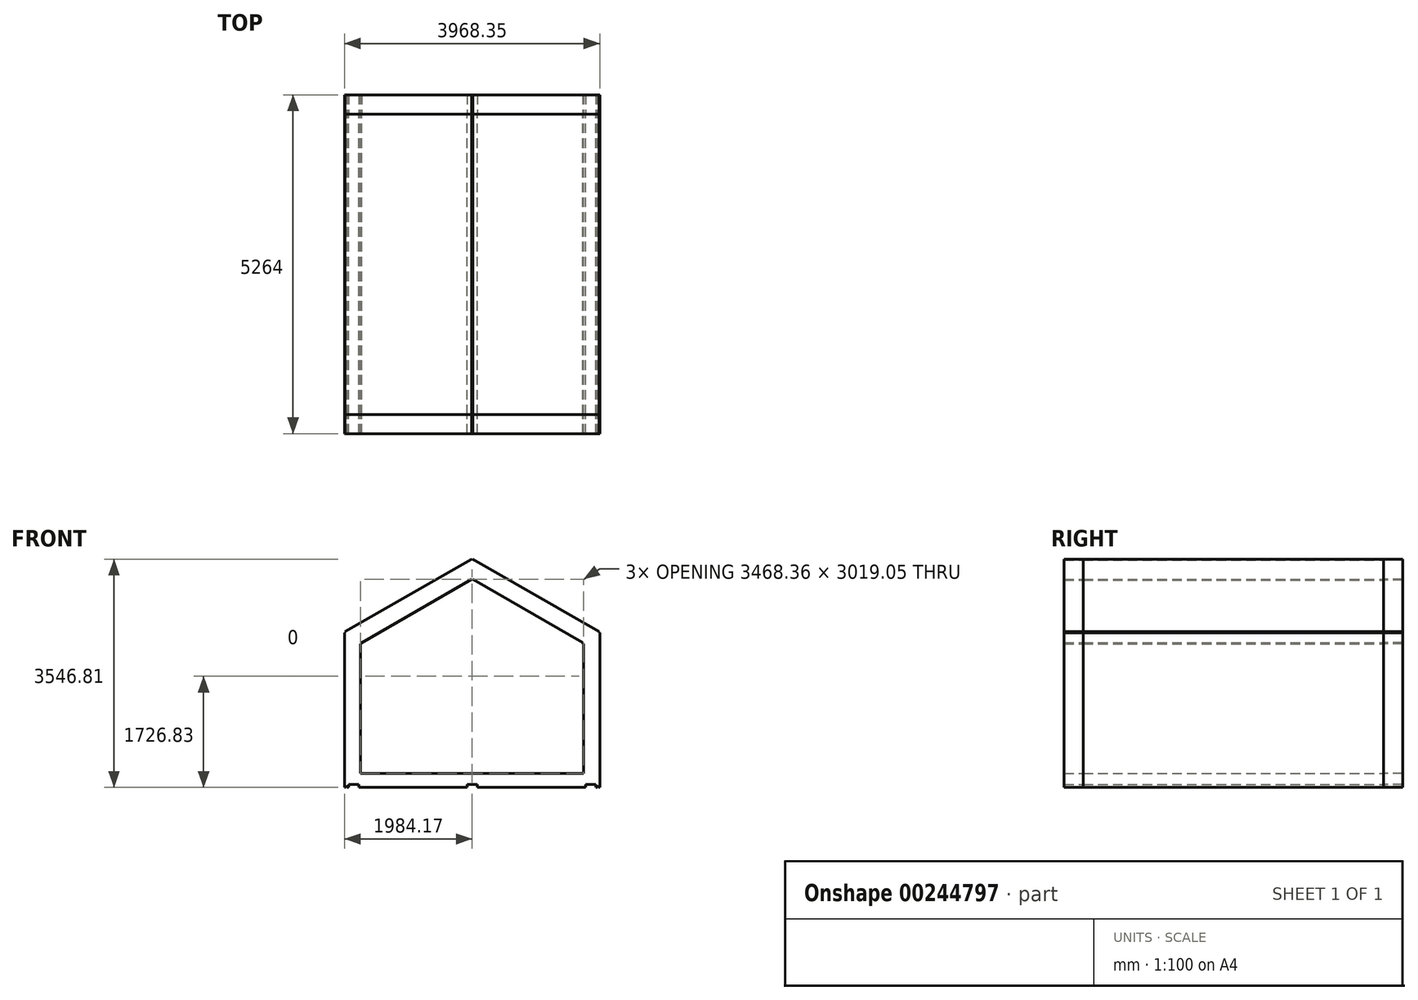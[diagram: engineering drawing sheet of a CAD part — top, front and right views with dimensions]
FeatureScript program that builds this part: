
annotation { "Feature Type Name" : "Feature", "Feature Type Description" : "" }
export const myFeature = defineFeature(function(context is Context, id is Id, definition is map)
    precondition{}
    {
        {
            var Q0;
            Q0=qCreatedBy(makeId("Front.planeOp"),FACE);
            var sketch = newSketch(context, id + "F0", { "sketchPlane" : qUnion([Q0])});
            skLineSegment(sketch, "E0", {"start": v(3294.63, -258.35) * mm, "end": v(3294.63, 2141.65) * mm});
            skLineSegment(sketch, "E1", {"start": v(3294.63, -258.35) * mm, "end": v(3312.63, -258.35) * mm});
            skLineSegment(sketch, "E2", {"start": v(3312.63, -258.35) * mm, "end": v(3312.63, 2141.65) * mm});
            skLineSegment(sketch, "E3", {"start": v(3294.63, -258.35) * mm, "end": v(3294.63, -244.35) * mm});
            skLineSegment(sketch, "E4", {"start": v(3294.63, -244.35) * mm, "end": v(3274.63, -244.35) * mm});
            skLineSegment(sketch, "E5", {"start": v(3294.63, -244.35) * mm, "end": v(3294.63, -258.35) * mm});
            skLineSegment(sketch, "E6", {"start": v(3274.63, -244.35) * mm, "end": v(3274.63, -262.35) * mm});
            skLineSegment(sketch, "E7", {"start": v(3274.63, -262.35) * mm, "end": v(3249.63, -262.35) * mm});
            skLineSegment(sketch, "E8", {"start": v(3249.63, -262.35) * mm, "end": v(3249.63, -212.35) * mm});
            skLineSegment(sketch, "E9", {"start": v(3249.63, -212.35) * mm, "end": v(3089.63, -212.35) * mm});
            skLineSegment(sketch, "E10", {"start": v(3089.63, -212.35) * mm, "end": v(3089.63, -262.35) * mm});
            skLineSegment(sketch, "E11", {"start": v(3089.63, -262.35) * mm, "end": v(1408.46, -262.35) * mm});
            skLineSegment(sketch, "E12", {"start": v(1408.46, -262.35) * mm, "end": v(1408.46, -212.35) * mm});
            skLineSegment(sketch, "E13", {"start": v(1408.46, -212.35) * mm, "end": v(1248.46, -212.35) * mm});
            skLineSegment(sketch, "E14", {"start": v(1248.46, -212.35) * mm, "end": v(1248.46, -262.35) * mm});
            skLineSegment(sketch, "E15", {"start": v(1248.46, -262.35) * mm, "end": v(-432.72, -262.35) * mm});
            skLineSegment(sketch, "E16", {"start": v(-432.72, -262.35) * mm, "end": v(-432.72, -212.35) * mm});
            skLineSegment(sketch, "E17", {"start": v(-432.72, -212.35) * mm, "end": v(-592.72, -212.35) * mm});
            skLineSegment(sketch, "E18", {"start": v(-592.72, -212.35) * mm, "end": v(-592.72, -262.35) * mm});
            skLineSegment(sketch, "E19", {"start": v(-592.72, -262.35) * mm, "end": v(-617.72, -262.35) * mm});
            skLineSegment(sketch, "E20", {"start": v(-617.72, -262.35) * mm, "end": v(-617.72, -244.35) * mm});
            skLineSegment(sketch, "E21", {"start": v(-617.72, -244.35) * mm, "end": v(-637.72, -244.35) * mm});
            skLineSegment(sketch, "E22", {"start": v(-637.72, -244.35) * mm, "end": v(-637.72, -258.35) * mm});
            skLineSegment(sketch, "E23", {"start": v(-637.72, -258.35) * mm, "end": v(-655.72, -258.35) * mm});
            skLineSegment(sketch, "E24", {"start": v(-655.72, -258.35) * mm, "end": v(-655.72, 2141.65) * mm});
            skLineSegment(sketch, "E25", {"start": v(-637.72, -244.35) * mm, "end": v(-637.72, 2141.68) * mm});
            skLineSegment(sketch, "E26", {"start": v(3294.63, 2141.65) * mm, "end": v(3312.63, 2141.65) * mm});
            skLineSegment(sketch, "E27", {"start": v(-637.72, 2141.68) * mm, "end": v(3294.63, 2141.65) * mm});
            skLineSegment(sketch, "E28", {"start": v(-637.72, 2141.68) * mm, "end": v(1328.46, 3268.85) * mm});
            skLineSegment(sketch, "E29", {"start": v(1328.46, 3268.85) * mm, "end": v(1319.5, 3284.46) * mm});
            skLineSegment(sketch, "E30", {"start": v(-655.72, 2141.65) * mm, "end": v(-637.72, 2141.68) * mm});
            skLineSegment(sketch, "E31", {"start": v(-637.72, 2141.68) * mm, "end": v(-649.03, 2161.4) * mm});
            skLineSegment(sketch, "E32", {"start": v(1328.46, -212.35) * mm, "end": v(1328.46, -9.04) * mm});
            skLineSegment(sketch, "E33", {"start": v(1328.46, -9.04) * mm, "end": v(-387.72, -9.03) * mm});
            skLineSegment(sketch, "E34", {"start": v(-387.72, -9.03) * mm, "end": v(-387.72, 1967.74) * mm});
            skLineSegment(sketch, "E35", {"start": v(1328.46, -9.04) * mm, "end": v(3044.63, -9.04) * mm});
            skLineSegment(sketch, "E36", {"start": v(3044.63, -9.04) * mm, "end": v(3044.63, 1967.73) * mm});
            skLineSegment(sketch, "E37", {"start": v(-649.03, 2161.4) * mm, "end": v(1319.5, 3284.46) * mm});
            skLineSegment(sketch, "E38", {"start": v(1328.46, 3268.85) * mm, "end": v(1328.46, 2958.42) * mm});
            skLineSegment(sketch, "E39", {"start": v(-387.72, 1967.74) * mm, "end": v(1328.46, 2958.42) * mm});
            skLineSegment(sketch, "E40", {"start": v(3044.63, 1967.73) * mm, "end": v(1328.46, 2958.42) * mm});
            skLineSegment(sketch, "E41", {"start": v(3044.63, 1967.73) * mm, "end": v(3062.63, 1967.73) * mm});
            skLineSegment(sketch, "E42", {"start": v(3062.63, 1967.73) * mm, "end": v(3044.63, 1967.73) * mm});
            skLineSegment(sketch, "E43", {"start": v(3044.63, 1967.73) * mm, "end": v(3044.63, 1985.73) * mm});
            skLineSegment(sketch, "E44", {"start": v(3062.63, -9.04) * mm, "end": v(3062.63, 1967.73) * mm});
            skLineSegment(sketch, "E45", {"start": v(1328.46, 2958.42) * mm, "end": v(1328.46, 2976.42) * mm});
            skLineSegment(sketch, "E46", {"start": v(1328.46, 3268.85) * mm, "end": v(3294.63, 2141.65) * mm});
            skPoint(sketch, "E47.endSnap0", {"position": v(3303.63, 2141.65) * mm});
            skLineSegment(sketch, "E48", {"start": v(3294.63, 2141.65) * mm, "end": v(3303.59, 2157.27) * mm});
            skLineSegment(sketch, "E49", {"start": v(1328.46, 3268.85) * mm, "end": v(1337.4, 3284.46) * mm});
            skLineSegment(sketch, "E50", {"start": v(1337.4, 3284.46) * mm, "end": v(3303.59, 2157.27) * mm});
            skLineSegment(sketch, "E51", {"start": v(1328.46, 2958.42) * mm, "end": v(1319.46, 2974) * mm});
            skLineSegment(sketch, "E52", {"start": v(1328.46, 2958.42) * mm, "end": v(1337.45, 2974) * mm});
            skLineSegment(sketch, "E53", {"start": v(1337.45, 2974) * mm, "end": v(3044.63, 1985.73) * mm});
            skLineSegment(sketch, "E54", {"start": v(-387.72, 1967.74) * mm, "end": v(-396.72, 1983.33) * mm});
            skLineSegment(sketch, "E55", {"start": v(-387.72, 1967.74) * mm, "end": v(-405.72, 1967.74) * mm});
            skLineSegment(sketch, "E56", {"start": v(-396.72, 1983.33) * mm, "end": v(1319.46, 2974) * mm});
            skLineSegment(sketch, "E57", {"start": v(-405.72, 1967.74) * mm, "end": v(-405.72, -9.03) * mm});
            skLineSegment(sketch, "E58.top", {"start": v(-405.72, -27.03) * mm, "end": v(-387.72, -27.03) * mm});
            skLineSegment(sketch, "E58.left", {"start": v(-405.72, -9.03) * mm, "end": v(-405.72, -27.03) * mm});
            skLineSegment(sketch, "E58.right", {"start": v(-387.72, -9.03) * mm, "end": v(-387.72, -27.03) * mm});
            skLineSegment(sketch, "E59.top", {"start": v(3044.63, -27.04) * mm, "end": v(3062.63, -27.04) * mm});
            skLineSegment(sketch, "E59.left", {"start": v(3044.63, -9.04) * mm, "end": v(3044.63, -27.04) * mm});
            skLineSegment(sketch, "E59.right", {"start": v(3062.63, -9.04) * mm, "end": v(3062.63, -27.04) * mm});
            skLineSegment(sketch, "E60", {"start": v(3044.63, -27.04) * mm, "end": v(-387.72, -27.03) * mm});
            skLineSegment(sketch, "E61", {"start": v(-405.72, -27.03) * mm, "end": v(-405.72, -45.03) * mm});
            skLineSegment(sketch, "E62", {"start": v(3062.63, -27.04) * mm, "end": v(3062.63, -45.04) * mm});
            skLineSegment(sketch, "E63", {"start": v(3062.63, -45.04) * mm, "end": v(-405.72, -45.03) * mm});
            skSolve(sketch);
        }
        {
            var Q0;
            Q0 = qSketchRegion(id + "F0", true);
            extrude(context, id + "F1", {"entities" : qUnion([Q0]), "depth" : 4664 * mm});
        }
        {
            var Q0;
            Q0=makeQuery(id+"F1.opExtrude","CAP_FACE",FACE,{"disambiguationData":[OSD([sQuery(id+"F0.wireOp",EDGE,"E1"),sQuery(id+"F0.wireOp",EDGE,"E2"),sQuery(id+"F0.wireOp",EDGE,"E4"),sQuery(id+"F0.wireOp",EDGE,"E5"),sQuery(id+"F0.wireOp",EDGE,"E6"),sQuery(id+"F0.wireOp",EDGE,"E7"),sQuery(id+"F0.wireOp",EDGE,"E8"),sQuery(id+"F0.wireOp",EDGE,"E9"),sQuery(id+"F0.wireOp",EDGE,"E10"),sQuery(id+"F0.wireOp",EDGE,"E11"),sQuery(id+"F0.wireOp",EDGE,"E12"),sQuery(id+"F0.wireOp",EDGE,"E13"),sQuery(id+"F0.wireOp",EDGE,"E14"),sQuery(id+"F0.wireOp",EDGE,"E15"),sQuery(id+"F0.wireOp",EDGE,"E16"),sQuery(id+"F0.wireOp",EDGE,"E17"),sQuery(id+"F0.wireOp",EDGE,"E18"),sQuery(id+"F0.wireOp",EDGE,"E19"),sQuery(id+"F0.wireOp",EDGE,"E20"),sQuery(id+"F0.wireOp",EDGE,"E21"),sQuery(id+"F0.wireOp",EDGE,"E22"),sQuery(id+"F0.wireOp",EDGE,"E23"),sQuery(id+"F0.wireOp",EDGE,"E24"),sQuery(id+"F0.wireOp",EDGE,"E26"),sQuery(id+"F0.wireOp",EDGE,"E29"),sQuery(id+"F0.wireOp",EDGE,"E30"),sQuery(id+"F0.wireOp",EDGE,"E31"),sQuery(id+"F0.wireOp",EDGE,"E37"),sQuery(id+"F0.wireOp",EDGE,"E42"),sQuery(id+"F0.wireOp",EDGE,"E43"),sQuery(id+"F0.wireOp",EDGE,"E44"),sQuery(id+"F0.wireOp",EDGE,"E48"),sQuery(id+"F0.wireOp",EDGE,"E49"),sQuery(id+"F0.wireOp",EDGE,"E50"),sQuery(id+"F0.wireOp",EDGE,"E51"),sQuery(id+"F0.wireOp",EDGE,"E52"),sQuery(id+"F0.wireOp",EDGE,"E53"),sQuery(id+"F0.wireOp",EDGE,"E54"),sQuery(id+"F0.wireOp",EDGE,"E55"),sQuery(id+"F0.wireOp",EDGE,"E56"),sQuery(id+"F0.wireOp",EDGE,"E57"),sQuery(id+"F0.wireOp",EDGE,"E58.top"),sQuery(id+"F0.wireOp",EDGE,"E58.left"),sQuery(id+"F0.wireOp",EDGE,"E59.top"),sQuery(id+"F0.wireOp",EDGE,"E59.right"),sQuery(id+"F0.wireOp",EDGE,"E60")])],"isStart":false});
            extrude(context, id + "F2", {"entities" : qUnion([Q0]), "depth" : 300 * mm});
        }
        {
            var Q0;
            Q0=makeQuery(id+"F1.opExtrude","CAP_FACE",FACE,{"disambiguationData":[OSD([sQuery(id+"F0.wireOp",EDGE,"E1"),sQuery(id+"F0.wireOp",EDGE,"E2"),sQuery(id+"F0.wireOp",EDGE,"E4"),sQuery(id+"F0.wireOp",EDGE,"E5"),sQuery(id+"F0.wireOp",EDGE,"E6"),sQuery(id+"F0.wireOp",EDGE,"E7"),sQuery(id+"F0.wireOp",EDGE,"E8"),sQuery(id+"F0.wireOp",EDGE,"E9"),sQuery(id+"F0.wireOp",EDGE,"E10"),sQuery(id+"F0.wireOp",EDGE,"E11"),sQuery(id+"F0.wireOp",EDGE,"E12"),sQuery(id+"F0.wireOp",EDGE,"E13"),sQuery(id+"F0.wireOp",EDGE,"E14"),sQuery(id+"F0.wireOp",EDGE,"E15"),sQuery(id+"F0.wireOp",EDGE,"E16"),sQuery(id+"F0.wireOp",EDGE,"E17"),sQuery(id+"F0.wireOp",EDGE,"E18"),sQuery(id+"F0.wireOp",EDGE,"E19"),sQuery(id+"F0.wireOp",EDGE,"E20"),sQuery(id+"F0.wireOp",EDGE,"E21"),sQuery(id+"F0.wireOp",EDGE,"E22"),sQuery(id+"F0.wireOp",EDGE,"E23"),sQuery(id+"F0.wireOp",EDGE,"E24"),sQuery(id+"F0.wireOp",EDGE,"E26"),sQuery(id+"F0.wireOp",EDGE,"E29"),sQuery(id+"F0.wireOp",EDGE,"E30"),sQuery(id+"F0.wireOp",EDGE,"E31"),sQuery(id+"F0.wireOp",EDGE,"E37"),sQuery(id+"F0.wireOp",EDGE,"E42"),sQuery(id+"F0.wireOp",EDGE,"E43"),sQuery(id+"F0.wireOp",EDGE,"E44"),sQuery(id+"F0.wireOp",EDGE,"E48"),sQuery(id+"F0.wireOp",EDGE,"E49"),sQuery(id+"F0.wireOp",EDGE,"E50"),sQuery(id+"F0.wireOp",EDGE,"E51"),sQuery(id+"F0.wireOp",EDGE,"E52"),sQuery(id+"F0.wireOp",EDGE,"E53"),sQuery(id+"F0.wireOp",EDGE,"E54"),sQuery(id+"F0.wireOp",EDGE,"E55"),sQuery(id+"F0.wireOp",EDGE,"E56"),sQuery(id+"F0.wireOp",EDGE,"E57"),sQuery(id+"F0.wireOp",EDGE,"E58.top"),sQuery(id+"F0.wireOp",EDGE,"E58.left"),sQuery(id+"F0.wireOp",EDGE,"E59.top"),sQuery(id+"F0.wireOp",EDGE,"E59.right"),sQuery(id+"F0.wireOp",EDGE,"E60")])],"isStart":true});
            extrude(context, id + "F3", {"entities" : qUnion([Q0]), "depth" : 300 * mm});
        }
    });
